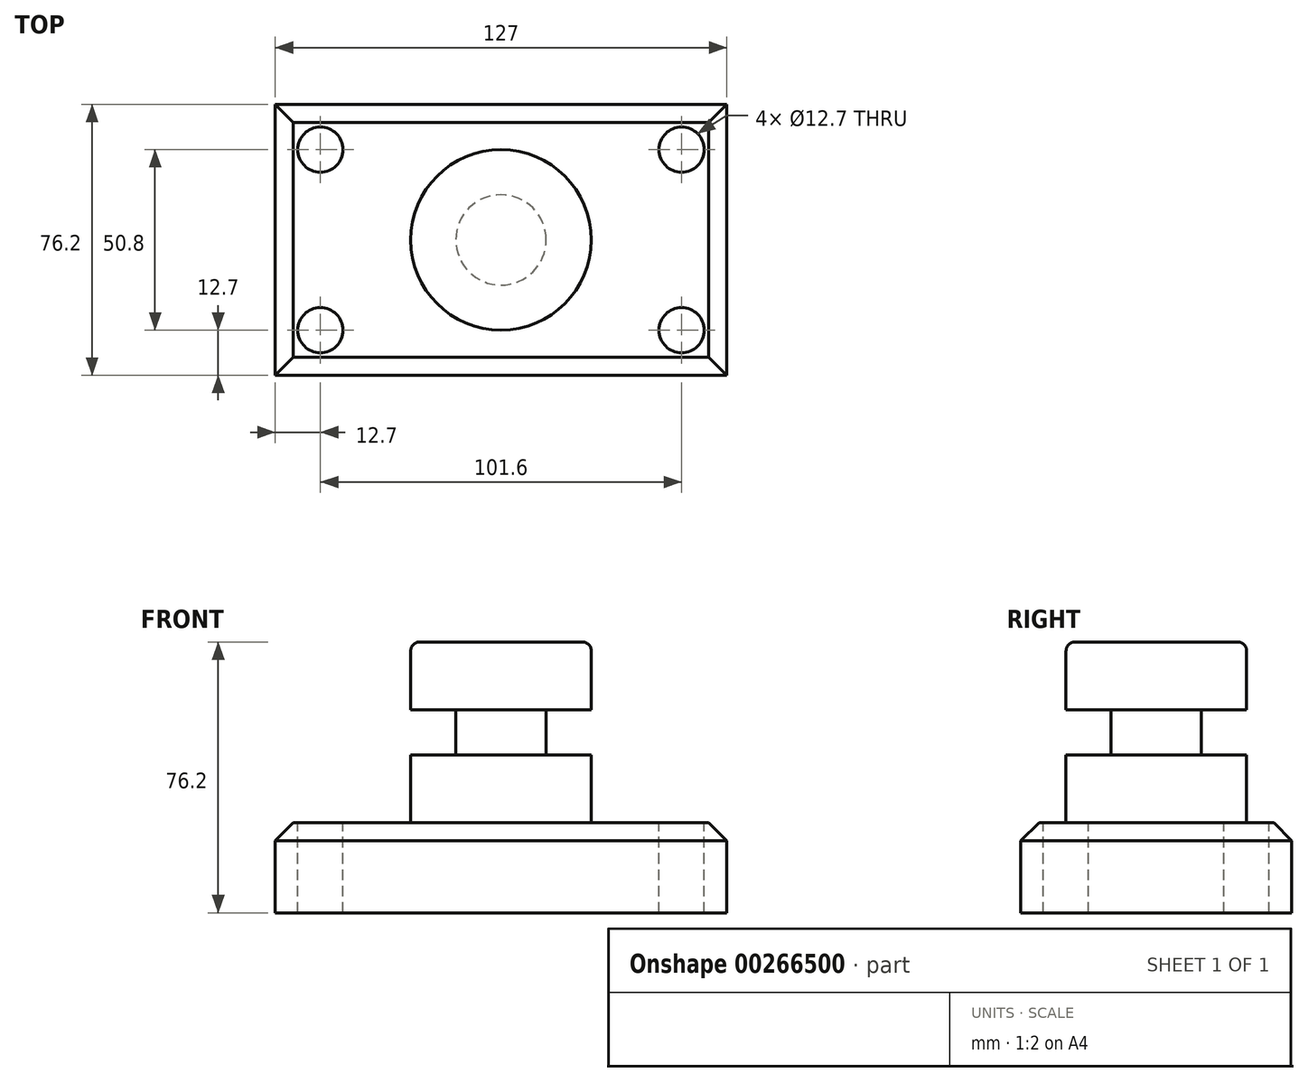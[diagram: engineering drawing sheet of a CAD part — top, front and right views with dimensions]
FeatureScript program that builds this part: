
annotation { "Feature Type Name" : "Feature", "Feature Type Description" : "" }
export const myFeature = defineFeature(function(context is Context, id is Id, definition is map)
    precondition{}
    {
        {
            var Q0;
            Q0=qCreatedBy(makeId("Top.planeOp"),FACE);
            var sketch = newSketch(context, id + "F0", { "sketchPlane" : qUnion([Q0])});
            skLineSegment(sketch, "E0.bottom", {"start": v(-63.5, -38.1) * mm, "end": v(63.5, -38.1) * mm});
            skLineSegment(sketch, "E0.top", {"start": v(-63.5, 38.1) * mm, "end": v(63.5, 38.1) * mm});
            skLineSegment(sketch, "E0.left", {"start": v(-63.5, -38.1) * mm, "end": v(-63.5, 38.1) * mm});
            skLineSegment(sketch, "E0.right", {"start": v(63.5, -38.1) * mm, "end": v(63.5, 38.1) * mm});
            skPoint(sketch, "E0.middle", {"position": v(0, 0) * mm});
            skSolve(sketch);
        }
        {
            var Q0;
            Q0=makeQuery(id+"F0.imprint","IMPRINT",FACE,{"disambiguationData":[TD([[makeQuery(id+"F0.imprint","IMPRINT",EDGE,{"derivedFrom":sQuery(id+"F0.wireOp",EDGE,"E0.bottom")}),1.0]])]});
            extrude(context, id + "F1", {"entities" : qUnion([Q0]), "depth" : 25.4 * mm});
        }
        {
            var Q0;
            Q0=makeQuery(id+"F1.opExtrude","CAP_FACE",FACE,{"disambiguationData":[OSD([sQuery(id+"F0.wireOp",EDGE,"E0.bottom"),sQuery(id+"F0.wireOp",EDGE,"E0.top"),sQuery(id+"F0.wireOp",EDGE,"E0.left"),sQuery(id+"F0.wireOp",EDGE,"E0.right")])],"isStart":false});
            var sketch = newSketch(context, id + "F2", { "sketchPlane" : qUnion([Q0])});
            skCircle(sketch, "E1", {"center": v(-50.8, 25.4) * mm, "radius": 6.35 * mm});
            skCircle(sketch, "E2", {"center": v(50.8, 25.4) * mm, "radius": 6.35 * mm});
            skCircle(sketch, "E3", {"center": v(-50.8, -25.4) * mm, "radius": 6.35 * mm});
            skCircle(sketch, "E4", {"center": v(50.8, -25.4) * mm, "radius": 6.35 * mm});
            skSolve(sketch);
        }
        {
            var Q0;
            Q0=makeQuery(id+"F2.imprint","IMPRINT",FACE,{"disambiguationData":[TD([[makeQuery(id+"F2.imprint","IMPRINT",EDGE,{"derivedFrom":sQuery(id+"F2.wireOp",EDGE,"E1")}),1.0]])]});
            var Q1;
            Q1=makeQuery(id+"F2.imprint","IMPRINT",FACE,{"disambiguationData":[TD([[makeQuery(id+"F2.imprint","IMPRINT",EDGE,{"derivedFrom":sQuery(id+"F2.wireOp",EDGE,"E2")}),1.0]])]});
            var Q2;
            Q2=makeQuery(id+"F2.imprint","IMPRINT",FACE,{"disambiguationData":[TD([[makeQuery(id+"F2.imprint","IMPRINT",EDGE,{"derivedFrom":sQuery(id+"F2.wireOp",EDGE,"E3")}),1.0]])]});
            var Q3;
            Q3=makeQuery(id+"F2.imprint","IMPRINT",FACE,{"disambiguationData":[TD([[makeQuery(id+"F2.imprint","IMPRINT",EDGE,{"derivedFrom":sQuery(id+"F2.wireOp",EDGE,"E4")}),1.0]])]});
            extrude(context, id + "F3", {"entities" : qUnion([Q0, Q1, Q2, Q3]), "operationType" : NewBodyOperationType.REMOVE, "oppositeDirection" : true, "depth" : 25.4 * mm});
        }
        {
            var Q0;
            Q0=qCreatedBy(makeId("Front.planeOp"),FACE);
            var sketch = newSketch(context, id + "F4", { "sketchPlane" : qUnion([Q0])});
            skLineSegment(sketch, "E5.bottom", {"start": v(0, 25.4) * mm, "end": v(-25.4, 25.4) * mm});
            skLineSegment(sketch, "E5.top", {"start": v(0, 76.2) * mm, "end": v(-25.4, 76.2) * mm});
            skLineSegment(sketch, "E5.left", {"start": v(0, 25.4) * mm, "end": v(0, 76.2) * mm});
            skLineSegment(sketch, "E5.right", {"start": v(-25.4, 25.4) * mm, "end": v(-25.4, 76.2) * mm});
            skSolve(sketch);
        }
        {
            var Q0;
            Q0=makeQuery(id+"F4.imprint","IMPRINT",FACE,{"disambiguationData":[TD([[makeQuery(id+"F4.imprint","IMPRINT",EDGE,{"derivedFrom":sQuery(id+"F4.wireOp",EDGE,"E5.bottom")}),-1.0]])]});
            var Q1;
            Q1=sQuery(id+"F4.wireOp",EDGE,"E5.left");
            revolve(context, id + "F5", {"operationType" : NewBodyOperationType.ADD, "entities" : qUnion([Q0]), "axis" : qUnion([Q1]), "revolveType" : RevolveType.FULL});
        }
        {
            var Q0;
            Q0=qCreatedBy(makeId("Front.planeOp"),FACE);
            var sketch = newSketch(context, id + "F6", { "sketchPlane" : qUnion([Q0])});
            skLineSegment(sketch, "E6.bottom", {"start": v(-40.87, 57.15) * mm, "end": v(-12.7, 57.15) * mm});
            skLineSegment(sketch, "E6.top", {"start": v(-40.87, 44.45) * mm, "end": v(-12.7, 44.45) * mm});
            skLineSegment(sketch, "E6.left", {"start": v(-40.87, 57.15) * mm, "end": v(-40.87, 44.45) * mm});
            skLineSegment(sketch, "E6.right", {"start": v(-12.7, 57.15) * mm, "end": v(-12.7, 44.45) * mm});
            skSolve(sketch);
        }
        {
            var Q0;
            Q0=makeQuery(id+"F6.imprint","IMPRINT",FACE,{"disambiguationData":[TD([[makeQuery(id+"F6.imprint","IMPRINT",EDGE,{"derivedFrom":sQuery(id+"F6.wireOp",EDGE,"E6.bottom")}),-1.0]])]});
            var Q1;
            Q1=makeQuery(id+"F5.opRevolve","SWEPT_FACE",FACE,{"disambiguationData":[OSD([sQuery(id+"F4.wireOp",EDGE,"E5.right")])]});
            revolve(context, id + "F7", {"operationType" : NewBodyOperationType.REMOVE, "entities" : qUnion([Q0]), "axis" : qUnion([Q1]), "revolveType" : RevolveType.FULL, "oppositeDirection" : true});
        }
        {
            var Q0;
            Q0=makeQuery(id+"F5.opRevolve","SWEPT_FACE",FACE,{"disambiguationData":[OSD([sQuery(id+"F4.wireOp",EDGE,"E5.top")])]});
            var Q1;
            Q1=makeQuery(id+"F5.opRevolve","SWEPT_EDGE",EDGE,{"disambiguationData":[OSD([sQuery(id+"F4.wireOp",EDGE,"E5.bottom"),sQuery(id+"F4.wireOp",EDGE,"E5.right")])]});
            fillet(context, id + "F8", {"entities" : qUnion([Q0, Q1]), "radius" : 2.54 * mm, "tangentPropagation" : true, "allowEdgeOverflow" : false});
        }
        {
            var Q0;
            Q0=makeQuery(id+"F1.opExtrude","CAP_EDGE",EDGE,{"disambiguationData":[OSD([sQuery(id+"F0.wireOp",EDGE,"E0.left")])],"isStart":false});
            var Q1;
            Q1=makeQuery(id+"F1.opExtrude","CAP_EDGE",EDGE,{"disambiguationData":[OSD([sQuery(id+"F0.wireOp",EDGE,"E0.bottom")])],"isStart":false});
            var Q2;
            Q2=makeQuery(id+"F1.opExtrude","CAP_EDGE",EDGE,{"disambiguationData":[OSD([sQuery(id+"F0.wireOp",EDGE,"E0.right")])],"isStart":false});
            var Q3;
            Q3=makeQuery(id+"F1.opExtrude","CAP_EDGE",EDGE,{"disambiguationData":[OSD([sQuery(id+"F0.wireOp",EDGE,"E0.top")])],"isStart":false});
            chamfer(context, id + "F9", {"entities" : qUnion([Q0, Q1, Q2, Q3]), "width" : 5.08 * mm, "tangentPropagation" : true});
        }
    });
